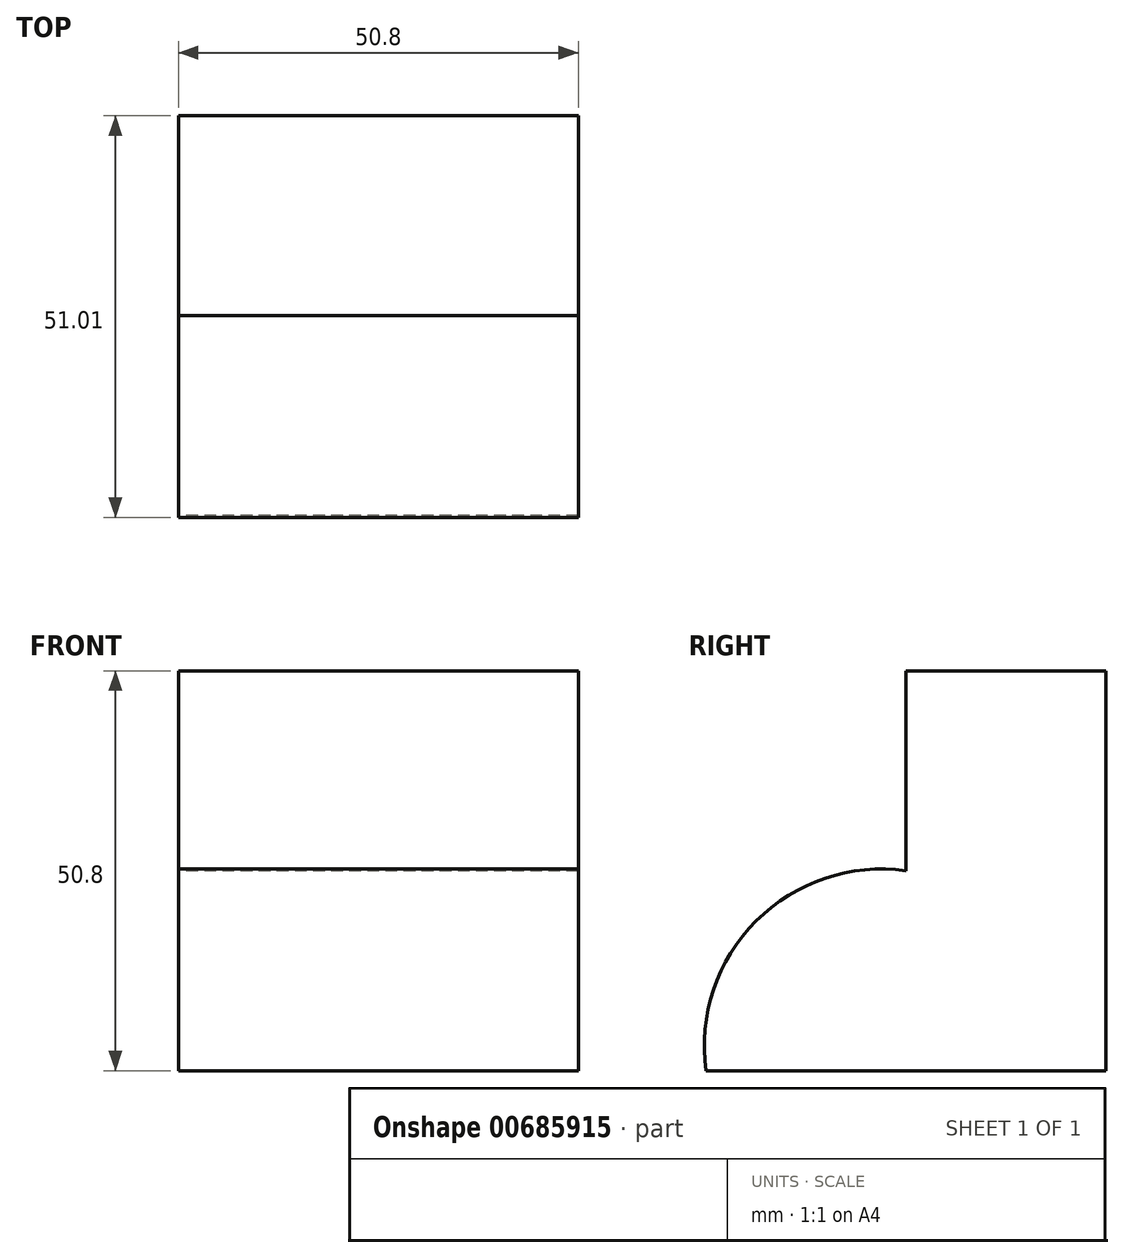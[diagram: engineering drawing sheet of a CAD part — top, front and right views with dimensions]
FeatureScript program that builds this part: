
annotation { "Feature Type Name" : "Feature", "Feature Type Description" : "" }
export const myFeature = defineFeature(function(context is Context, id is Id, definition is map)
    precondition{}
    {
        {
            var Q0;
            Q0=qCreatedBy(makeId("Right.planeOp"),FACE);
            var sketch = newSketch(context, id + "F0", { "sketchPlane" : qUnion([Q0])});
            skLineSegment(sketch, "E0", {"start": v(0, -38.1) * mm, "end": v(50.8, -38.1) * mm});
            skLineSegment(sketch, "E1", {"start": v(50.8, -38.1) * mm, "end": v(50.8, 12.7) * mm});
            skLineSegment(sketch, "E2", {"start": v(50.8, 12.7) * mm, "end": v(25.4, 12.7) * mm});
            skLineSegment(sketch, "E3", {"start": v(25.4, 12.7) * mm, "end": v(25.4, -12.7) * mm});
            skArc(sketch, "E4", {"start": v(25.4, -12.7) * mm, "mid": v(6.39, -19.08) * mm, "end": v(0, -38.1) * mm});
            skSolve(sketch);
        }
        {
            var Q0;
            Q0 = qSketchRegion(id + "F0", true);
            extrude(context, id + "F1", {"entities" : qUnion([Q0]), "depth" : 50.8 * mm, "offsetDistance" : 25.4 * mm});
        }
    });
